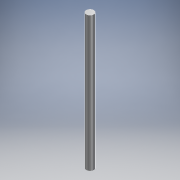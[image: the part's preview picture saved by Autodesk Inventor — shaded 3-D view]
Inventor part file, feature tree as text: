
AUTODESK INVENTOR PART (.ipt)
format: ipt  version: 2016 (Build 200138000, 138)  size: 89,600 bytes
history: native  units: mm
features: extrude x1, thread x1, sketch x1, reference x1
ambient origin geometry x8: Origin, YZ Plane, XZ Plane, XY Plane, X Axis, Y Axis, Z Axis, Center Point
bodies: Solid1 (feature_tree)
feature tree (4):
  extrude  "Extrusion1"  Depth=10.0mm
  thread  "Thread1"  [1 undecoded]
  sketch  "Sketch1"  dims[d0=140.0mm d1=0.0mm d2=8.0mm d3=10.0mm d4=0.0mm]
  reference  "Reference1"
note: 1 required parameter value undecoded (feature->parameter linkage not recoverable at this tier; creation-order binding heuristic only, values carry confidence <= 0.55)
